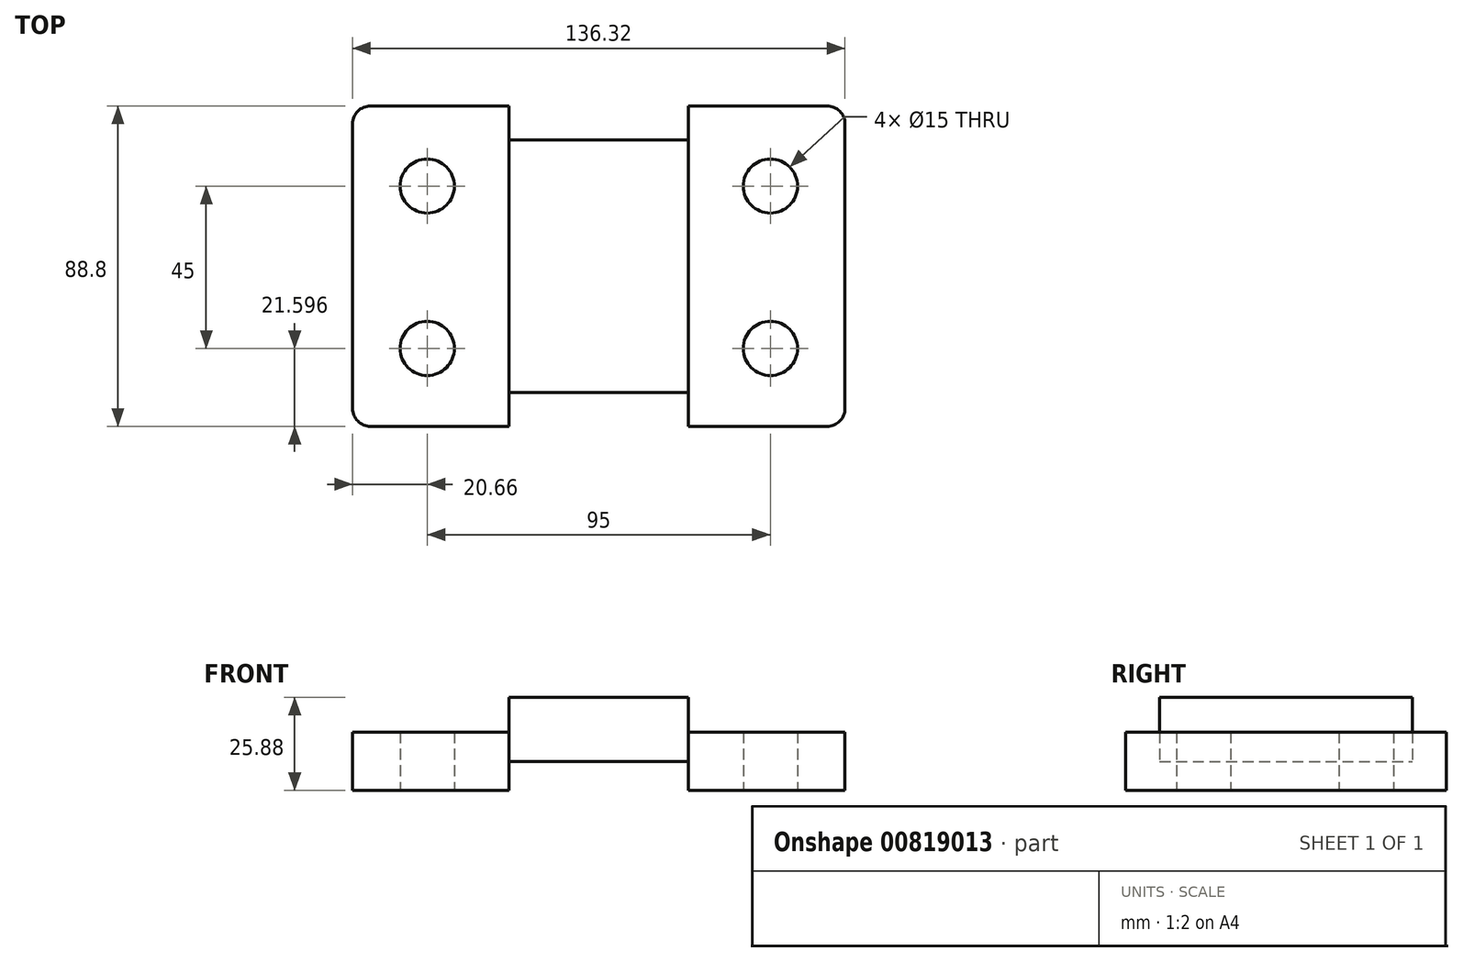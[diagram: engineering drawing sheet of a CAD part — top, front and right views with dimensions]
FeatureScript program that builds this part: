
annotation { "Feature Type Name" : "Feature", "Feature Type Description" : "" }
export const myFeature = defineFeature(function(context is Context, id is Id, definition is map)
    precondition{}
    {
        {
            var Q0;
            Q0=qCreatedBy(makeId("Top.planeOp"),FACE);
            var sketch = newSketch(context, id + "F0", { "sketchPlane" : qUnion([Q0])});
            skLineSegment(sketch, "E0.bottom", {"start": v(0, -35) * mm, "end": v(-24.82, -35) * mm});
            skLineSegment(sketch, "E0.top", {"start": v(0, 35) * mm, "end": v(-24.82, 35) * mm});
            skLineSegment(sketch, "E0.left", {"start": v(0, -35) * mm, "end": v(0, 35) * mm});
            skLineSegment(sketch, "E0.right", {"start": v(-24.82, -35) * mm, "end": v(-24.82, 35) * mm});
            skLineSegment(sketch, "E1.bottom", {"start": v(-24.82, -44.4) * mm, "end": v(-63.16, -44.4) * mm});
            skLineSegment(sketch, "E1.top", {"start": v(-24.82, 44.4) * mm, "end": v(-63.16, 44.4) * mm});
            skLineSegment(sketch, "E1.left", {"start": v(-24.82, -44.4) * mm, "end": v(-24.82, 44.4) * mm});
            skLineSegment(sketch, "E1.right", {"start": v(-68.15, -39.4) * mm, "end": v(-68.15, 39.4) * mm});
            skLineSegment(sketch, "E2.MirrorCS", {"start": v(24.82, -35) * mm, "end": v(24.82, 35) * mm});
            skLineSegment(sketch, "E3.MirrorCS", {"start": v(0, 35) * mm, "end": v(24.82, 35) * mm});
            skLineSegment(sketch, "E4.MirrorCS", {"start": v(24.82, 44.4) * mm, "end": v(63.15, 44.4) * mm});
            skLineSegment(sketch, "E5.MirrorCS", {"start": v(24.82, -44.4) * mm, "end": v(63.15, -44.4) * mm});
            skLineSegment(sketch, "E6.MirrorCS", {"start": v(68.16, -39.4) * mm, "end": v(68.15, 39.4) * mm});
            skLineSegment(sketch, "E7.MirrorCS", {"start": v(0, -35) * mm, "end": v(24.82, -35) * mm});
            skLineSegment(sketch, "E8.MirrorCS", {"start": v(24.82, -44.4) * mm, "end": v(24.82, 44.4) * mm});
            skPoint(sketch, "E9.visualSharp", {"position": v(-68.16, -44.4) * mm});
            skArc(sketch, "E9.filletArc", {"start": v(-68.16, -39.4) * mm, "mid": v(-66.7, -42.93) * mm, "end": v(-63.16, -44.4) * mm});
            skPoint(sketch, "E10.visualSharp", {"position": v(-68.16, 44.4) * mm});
            skArc(sketch, "E10.filletArc", {"start": v(-63.16, 44.4) * mm, "mid": v(-66.7, 42.93) * mm, "end": v(-68.16, 39.4) * mm});
            skPoint(sketch, "E11.visualSharp", {"position": v(68.16, -44.4) * mm});
            skArc(sketch, "E11.filletArc", {"start": v(63.15, -44.4) * mm, "mid": v(66.7, -42.93) * mm, "end": v(68.15, -39.4) * mm});
            skPoint(sketch, "E12.visualSharp", {"position": v(68.16, 44.4) * mm});
            skArc(sketch, "E12.filletArc", {"start": v(68.15, 39.4) * mm, "mid": v(66.7, 42.93) * mm, "end": v(63.15, 44.4) * mm});
            skCircle(sketch, "E13", {"center": v(-47.5, -22.8) * mm, "radius": 7.5 * mm});
            skCircle(sketch, "E14", {"center": v(-47.5, 22.2) * mm, "radius": 7.5 * mm});
            skCircle(sketch, "E15.MirrorC", {"center": v(47.5, 22.2) * mm, "radius": 7.5 * mm});
            skCircle(sketch, "E16.MirrorC", {"center": v(47.5, -22.8) * mm, "radius": 7.5 * mm});
            skSolve(sketch);
        }
        {
            var Q0;
            Q0=makeQuery(id+"F0.imprint","IMPRINT",FACE,{"disambiguationData":[TD([[makeQuery(id+"F0.imprint","IMPRINT",EDGE,{"derivedFrom":sQuery(id+"F0.wireOp",EDGE,"E0.left")}),-1.0]])]});
            var Q1;
            {var subQ0=sQuery(id+"F0.wireOp",EDGE,"E0.bottom");Q1=makeQuery(id+"F0.imprint","IMPRINT",FACE,{"disambiguationData":[TD([[makeQuery(id+"F0.imprint","IMPRINT",EDGE,{"derivedFrom":subQ0}),-1.0]])]});}
            extrude(context, id + "F1", {"entities" : qUnion([Q0, Q1]), "depth" : 17.79 * mm, "offsetDistance" : 25 * mm});
        }
        {
            var Q0;
            {var subQ3=sQuery(id+"F0.wireOp",EDGE,"E4.MirrorCS");Q0=makeQuery(id+"F0.imprint","IMPRINT",FACE,{"disambiguationData":[TD([[makeQuery(id+"F0.imprint","IMPRINT",EDGE,{"derivedFrom":subQ3}),-1.0]])]});}
            var Q1;
            {var subQ3=sQuery(id+"F0.wireOp",EDGE,"E1.bottom");Q1=makeQuery(id+"F0.imprint","IMPRINT",FACE,{"disambiguationData":[TD([[makeQuery(id+"F0.imprint","IMPRINT",EDGE,{"derivedFrom":subQ3}),-1.0]])]});}
            extrude(context, id + "F2", {"entities" : qUnion([Q0, Q1]), "operationType" : NewBodyOperationType.ADD, "depth" : 8.1 * mm, "offsetDistance" : 25 * mm});
        }
        {
            var Q0;
            {var subQ3=sQuery(id+"F0.wireOp",EDGE,"E1.bottom");Q0=makeQuery(id+"F0.imprint","IMPRINT",FACE,{"disambiguationData":[TD([[makeQuery(id+"F0.imprint","IMPRINT",EDGE,{"derivedFrom":subQ3}),-1.0]])]});}
            var Q1;
            {var subQ3=sQuery(id+"F0.wireOp",EDGE,"E4.MirrorCS");Q1=makeQuery(id+"F0.imprint","IMPRINT",FACE,{"disambiguationData":[TD([[makeQuery(id+"F0.imprint","IMPRINT",EDGE,{"derivedFrom":subQ3}),-1.0]])]});}
            extrude(context, id + "F3", {"entities" : qUnion([Q0, Q1]), "operationType" : NewBodyOperationType.ADD, "oppositeDirection" : true, "depth" : 8.1 * mm, "offsetDistance" : 25 * mm});
        }
    });
